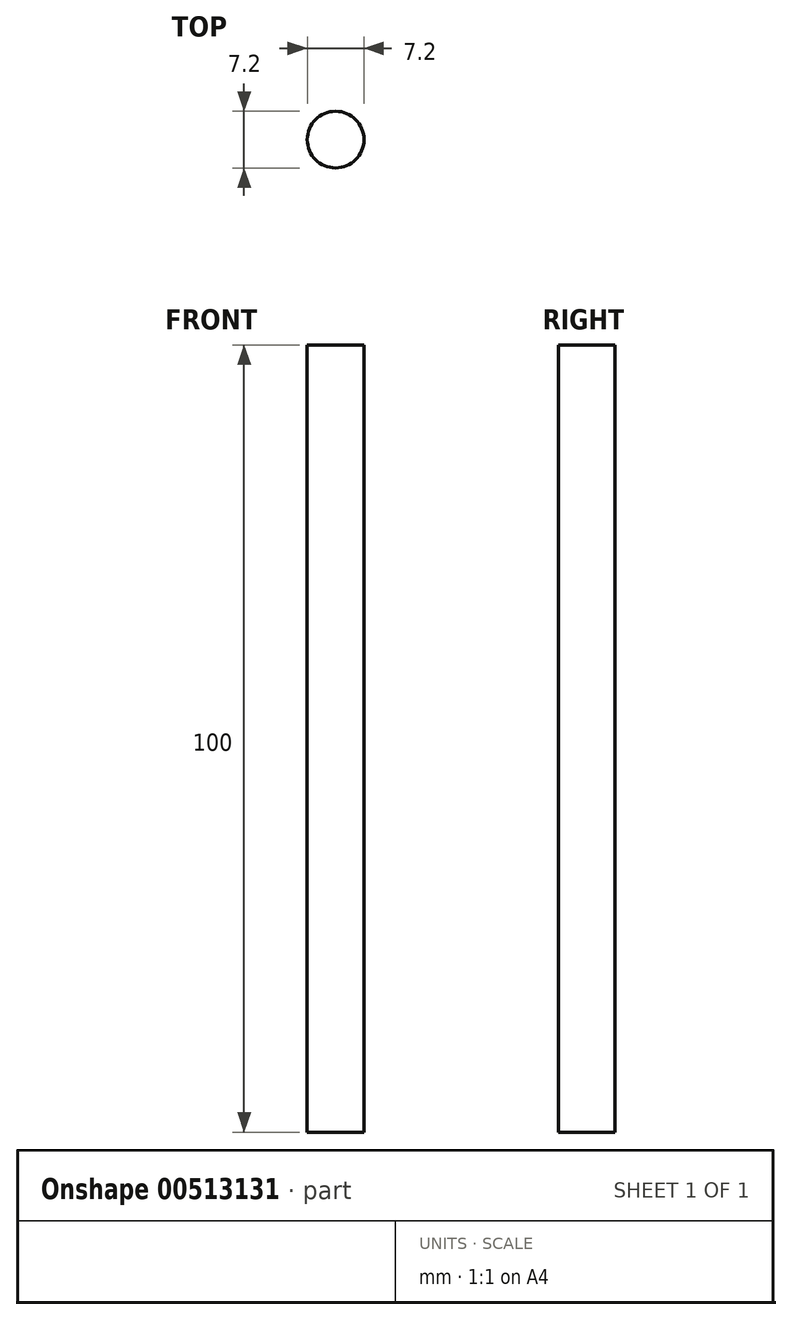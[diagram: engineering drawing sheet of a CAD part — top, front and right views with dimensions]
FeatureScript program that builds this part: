
annotation { "Feature Type Name" : "Feature", "Feature Type Description" : "" }
export const myFeature = defineFeature(function(context is Context, id is Id, definition is map)
    precondition{}
    {
        {
            var Q0;
            Q0=qCreatedBy(makeId("Top.planeOp"),FACE);
            var sketch = newSketch(context, id + "F0", { "sketchPlane" : qUnion([Q0])});
            skCircle(sketch, "E0", {"center": v(-24, 14.86) * mm, "radius": 3.6 * mm});
            skSolve(sketch);
        }
        {
            var Q0;
            Q0=makeQuery(id+"F0.imprint","IMPRINT",FACE,{"disambiguationData":[TD([[makeQuery(id+"F0.imprint","IMPRINT",EDGE,{"derivedFrom":sQuery(id+"F0.wireOp",EDGE,"E0")}),1.0]])]});
            extrude(context, id + "F1", {"entities" : qUnion([Q0]), "depth" : 100 * mm});
        }
    });
